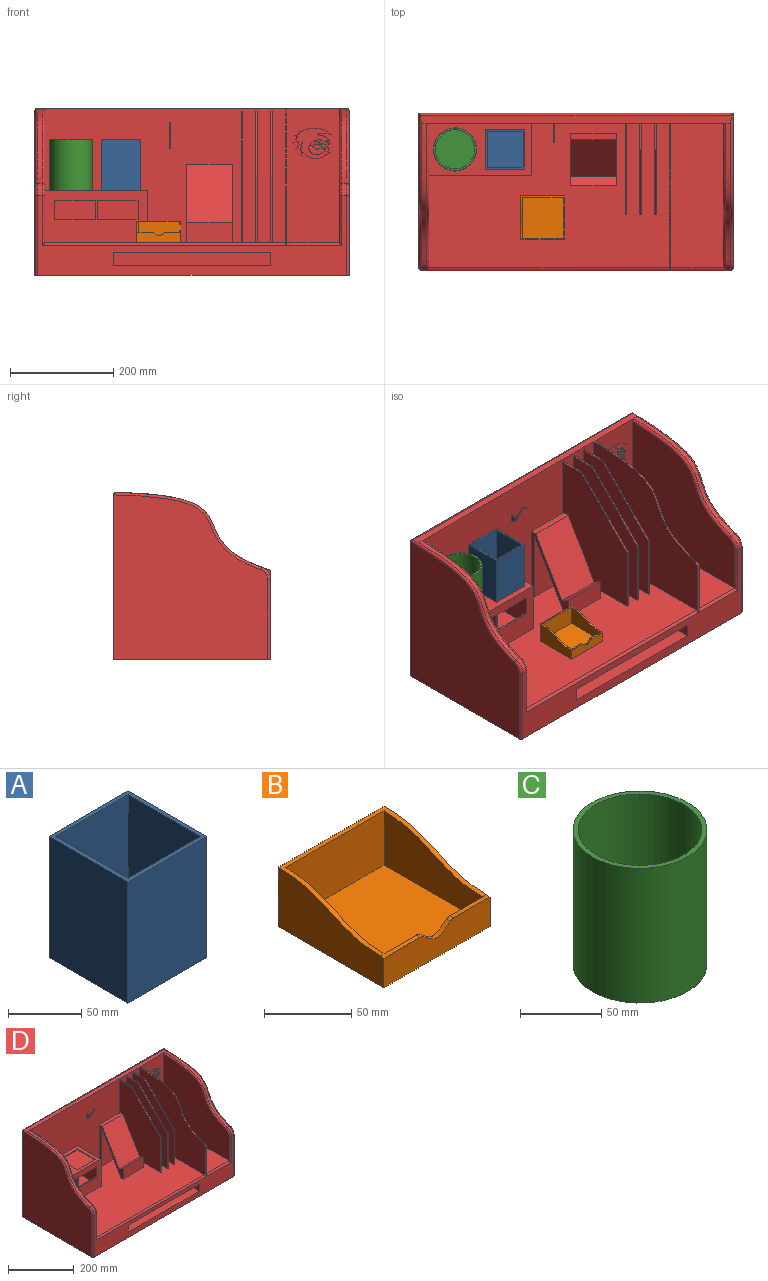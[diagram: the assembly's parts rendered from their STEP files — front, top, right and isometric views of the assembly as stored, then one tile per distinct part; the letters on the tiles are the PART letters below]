
ASSEMBLY  parts=4 mates=3
PART A: 11 faces, bbox 76.2x76.2x101.6 mm
  f0: plane 101.6x76.2mm, normal (-1,0,0), area 7741.9mm2, adj f1,f3,f4,f5
  f1: plane 101.6x76.2mm, normal (0,-1,0), area 7741.9mm2, adj f0,f2,f4,f5
  f2: plane 101.6x76.2mm, normal (1,0,0), area 7741.9mm2, adj f1,f3,f4,f5
  f3: plane 101.6x76.2mm, normal (0,1,0), area 7741.9mm2, adj f0,f2,f4,f5
  f4: plane 76.2x76.2mm, normal (0,0,1), area 927.4mm2, adj f0,f1,f2,f3,f6,f7,f8,f9
  f5: plane 76.2x76.2mm, normal (0,0,-1), area 5806.4mm2, adj f0,f1,f2,f3
  f6: plane 98.43x69.85mm, normal (1,0,0), area 6875mm2, adj f4,f7,f9,f10
  f7: plane 98.43x69.85mm, normal (0,1,0), area 6875mm2, adj f4,f6,f8,f10
  f8: plane 98.43x69.85mm, normal (-1,0,0), area 6875mm2, adj f4,f7,f9,f10
  f9: plane 98.43x69.85mm, normal (0,-1,0), area 6875mm2, adj f4,f6,f8,f10
  f10: plane 69.85x69.85mm, normal (0,0,1), area 4879mm2, adj f6,f7,f8,f9
PART B: 18 faces, bbox 85.7x85.7x41.3 mm
  f0: plane 79.38x17.46mm, normal (0,1,0), area 1283.4mm2, adj f7,f9,f10,f11,f13,f15,f16,f17
  f1: plane 85.73x41.28mm, normal (1,0,0), area 2661mm2, adj f2,f3,f5,f6,f14,f15
  f2: extruded ~85.73x82.55mm, area 797.9mm2, adj f1,f4,f5,f8,f9,f10,f12,f14
  f3: plane 85.73x20.64mm, normal (0,-1,0), area 1666.5mm2, adj f1,f4,f6,f11,f13,f15,f16,f17
  f4: plane 85.73x41.28mm, normal (-1,0,0), area 2661mm2, adj f2,f3,f5,f6,f12,f13
  f5: plane 85.73x41.28mm, normal (0,1,0), area 3538.3mm2, adj f1,f2,f4,f6
  f6: plane 85.73x85.73mm, normal (0,0,-1), area 7348.8mm2, adj f1,f3,f4,f5
  f7: plane 79.38x79.38mm, normal (0,0,1), area 6300.4mm2, adj f0,f8,f9,f10
  f8: plane 79.38x38.06mm, normal (0,-1,0), area 3021.2mm2, adj f2,f7,f9,f10
  f9: plane 85.73x38.1mm, normal (-1,0,0), area 2212.5mm2, adj f0,f2,f7,f8,f14
  f10: plane 85.73x38.1mm, normal (1,0,0), area 2212.5mm2, adj f0,f2,f7,f8,f12
  f11: extruded ~21.25x6.04mm, area 78.7mm2, adj f0,f3,f16,f17
  f12: plane 3.18x0.04mm, normal (0,-1,0), area 0.1mm2, adj f2,f4,f10,f13
  f13: plane 29.06x3.18mm, normal (0,0,1), area 92.3mm2, adj f0,f3,f4,f12,f16
  f14: plane 3.18x0.04mm, normal (0,-1,0), area 0.1mm2, adj f1,f2,f9,f15
  f15: plane 29.14x3.18mm, normal (0,0,1), area 92.5mm2, adj f0,f1,f3,f14,f17
  f16: cylinder r=5.08mm len=3.19mm, axis (0,-1,0), area 11mm2, adj f0,f3,f11,f13
  f17: cylinder r=5.08mm len=3.18mm, axis (0,-1,0), area 10.5mm2, adj f0,f3,f11,f15
PART C: 5 faces, bbox 82.6x82.6x101.6 mm
  f0: cylinder r=38.1mm len=98.43mm, axis (0,0,-1), area 23561.9mm2, adj f1,f4
  f1: plane 76.2x76.2mm, normal (0,0,1), area 4560.4mm2, adj f0
  f2: plane 82.55x82.55mm, normal (0,0,-1), area 5352.1mm2, adj f3
  f3: cylinder r=41.27mm len=101.6mm, axis (0,0,-1), area 26348.8mm2, adj f2,f4
  f4: plane 82.55x82.55mm, normal (0,0,1), area 791.7mm2, adj f0,f3
PART D: 129 faces, bbox 610.7x318.8x325.8 mm
  f0: plane 24.63x18.14mm, normal (-1,0,0), area 108.7mm2, adj f2,f127,f128
  f1: plane 24.63x18.14mm, normal (1,0,0), area 108.7mm2, adj f2,f125,f126
  f2: plane 472.26x260.81mm, normal (0,-1,0), area 98721.5mm2, adj f0,f1,f7,f8,f14,f15,f57,f59
  f3: plane 79.38x3.18mm, normal (0,0,1), area 252mm2, adj f79,f109,f110,f113
  f4: plane 79.38x3.18mm, normal (0,0,1), area 252mm2, adj f79,f103,f104,f107
  f5: plane 152.4x101.6mm, normal (-1,0,0), area 2847.1mm2, adj f7,f81,f82,f83,f84,f85,f86,f87
  f6: plane 152.4x101.6mm, normal (1,0,0), area 2847.1mm2, adj f7,f81,f82,f83,f84,f85,f86,f87
  f7: plane 466.73x280.67mm, normal (0,0,1), area 107438.7mm2, adj f2,f5,f6,f8,f15,f57,f58,f59
  f8: plane 280.69x255.29mm, normal (1,0,0), area 45920.9mm2, adj f2,f7,f79,f80,f88,f89,f91
  f9: plane 260.53x106.86mm, normal (0,-1,0), area 23716.6mm2, adj f13,f14,f16,f22,f33,f34,f35,f36
  f10: plane 319.37x299.72mm, normal (-1,0,0), area 80145.8mm2, adj f20,f21,f96,f97,f98,f99
  f11: plane 319.37x299.72mm, normal (1,0,0), area 80145.8mm2, adj f20,f21,f99,f100,f101,f102
  f12: plane 599.44x173.06mm, normal (0,-1,0), area 29355mm2, adj f15,f16,f17,f18,f21,f23,f24,f25
  f13: plane 280.69x255.29mm, normal (-1,0,0), area 56243.5mm2, adj f9,f22,f92,f93,f95
  f14: plane 604.6x15.06mm, normal (0,0,1), area 8412.6mm2, adj f2,f9,f25,f26,f27,f98,f99,f100
  f15: plane 285.75x265.43mm, normal (-1,0,0), area 58574mm2, adj f2,f7,f12,f25,f90
  f16: plane 285.75x265.43mm, normal (1,0,0), area 58574mm2, adj f9,f12,f22,f25,f94
  f17: plane 304.8x215.9mm, normal (0,0,1), area 65806.3mm2, adj f12,f19,f23,f24
  f18: plane 304.8x215.9mm, normal (0,0,-1), area 65806.3mm2, adj f12,f19,f23,f24
  f19: plane 304.8x25.4mm, normal (0,-1,0), area 7741.9mm2, adj f17,f18,f23,f24
  f20: plane 609.6x318.77mm, normal (0,1,0), area 194322.2mm2, adj f10,f11,f21,f99
  f21: plane 609.6x304.8mm, normal (0,0,-1), area 185795mm2, adj f10,f11,f12,f20,f96,f102
  f22: plane 280.67x101.6mm, normal (0,0,1), area 28516.1mm2, adj f9,f13,f16,f94
  f23: plane 215.9x25.4mm, normal (1,0,0), area 5483.9mm2, adj f12,f17,f18,f19
  f24: plane 215.9x25.4mm, normal (-1,0,0), area 5483.9mm2, adj f12,f17,f18,f19
  f25: extruded ~285.75x150.79mm, area 1094.7mm2, adj f12,f14,f15,f16
  f26: extruded ~268.97x145.16mm, area 2907.8mm2, adj f14,f29,f88,f98
  f27: extruded ~268.97x145.16mm, area 2907.8mm2, adj f14,f28,f92,f100
  f28: cylinder r=25.4mm len=23.89mm, axis (1,0,0), area 276.5mm2, adj f12,f27,f93,f101
  f29: cylinder r=25.4mm len=23.89mm, axis (1,0,0), area 276.5mm2, adj f12,f26,f89,f97
  f30: extruded ~3.81x2.23mm, area 13mm2, adj f52,f53,f56
  f31: extruded ~15.99x3.81mm, area 72.7mm2, adj f32,f49,f53,f55
  f32: extruded ~31.93x17.85mm, area 177.4mm2, adj f31,f49,f53,f55
  f33: extruded ~28.35x17.13mm, area 198.3mm2, adj f9,f34,f50,f53
  f34: extruded ~12.32x3.88mm, area 60.3mm2, adj f9,f33,f35,f53
  f35: extruded ~61.37x13.22mm, area 353.4mm2, adj f9,f34,f36,f53
  f36: extruded ~9.17x7.63mm, area 47.9mm2, adj f9,f35,f37,f53
  f37: extruded ~14.68x8.43mm, area 80mm2, adj f9,f36,f38,f53
  f38: extruded ~16.13x11.02mm, area 109.9mm2, adj f9,f37,f39,f53
  f39: extruded ~16.72x13.57mm, area 144.1mm2, adj f9,f38,f40,f53
  f40: extruded ~13.33x3.81mm, area 70.6mm2, adj f9,f39,f41,f53
  f41: extruded ~51.25x13.41mm, area 244mm2, adj f9,f40,f42,f53
  f42: extruded ~4.5x3.81mm, area 21.8mm2, adj f9,f41,f43,f53
  f43: extruded ~5.17x4mm, area 25.1mm2, adj f9,f42,f50,f53
  f44: extruded ~5.57x5.27mm, area 29.5mm2, adj f45,f51,f53,f54
  f45: extruded ~24.26x14.85mm, area 116.3mm2, adj f44,f46,f53,f54
  f46: extruded ~11.34x8.7mm, area 62.2mm2, adj f45,f47,f53,f54
  f47: extruded ~10.16x3.81mm, area 46.3mm2, adj f46,f48,f53,f54
  f48: extruded ~5.23x4.75mm, area 27mm2, adj f47,f51,f53,f54
  f49: extruded ~15.73x8.64mm, area 68.9mm2, adj f31,f32,f53,f55
  f50: extruded ~26.47x19.58mm, area 138mm2, adj f9,f33,f43,f53
  f51: extruded ~6x3.82mm, area 27.9mm2, adj f44,f48,f53,f54
  f52: extruded ~3.81x2.38mm, area 14.7mm2, adj f30,f53,f56
  f53: plane 74.8x59.57mm, normal (0,-1,0), area 2258.7mm2, adj f30,f31,f32,f33,f34,f35,f36,f37
  f54: plane 29.84x14.86mm, normal (0,-1,0), area 151.1mm2, adj f44,f45,f46,f47,f48,f51
  f55: plane 31.99x17.9mm, normal (0,-1,0), area 322.3mm2, adj f31,f32,f49
  f56: plane 2.94x2.91mm, normal (0,-1,0), area 3.4mm2, adj f30,f52
  f57: plane 254x177.8mm, normal (-1,0,0), area 37095.6mm2, adj f2,f7,f58,f60,f71,f72,f73
  f58: plane 124.9x3.18mm, normal (0,-1,0), area 396.5mm2, adj f7,f57,f59,f73
  f59: plane 254x177.8mm, normal (1,0,0), area 37095.6mm2, adj f2,f7,f58,f60,f71,f72,f73
  f60: plane 48.7x3.18mm, normal (0,0,1), area 154.6mm2, adj f2,f57,f59,f72
  f61: plane 254x177.8mm, normal (-1,0,0), area 37095.6mm2, adj f2,f7,f62,f64,f70,f74,f75
  f62: plane 124.9x3.18mm, normal (0,-1,0), area 396.5mm2, adj f7,f61,f63,f75
  f63: plane 254x177.8mm, normal (1,0,0), area 37095.6mm2, adj f2,f7,f62,f64,f70,f74,f75
  f64: plane 48.7x3.18mm, normal (0,0,1), area 154.6mm2, adj f2,f61,f63,f74
  f65: plane 254x177.8mm, normal (-1,0,0), area 37095.6mm2, adj f2,f7,f66,f68,f69,f76,f77
  f66: plane 124.9x3.18mm, normal (0,-1,0), area 396.5mm2, adj f7,f65,f67,f77
  f67: plane 254x177.8mm, normal (1,0,0), area 37095.6mm2, adj f2,f7,f66,f68,f69,f76,f77
  f68: plane 48.7x3.18mm, normal (0,0,1), area 154.6mm2, adj f2,f65,f67,f76
  f69: plane 124.02x124.02mm, normal (0,-0.71,0.71), area 556.9mm2, adj f65,f67,f76,f77
  f70: plane 124.02x124.02mm, normal (0,-0.71,0.71), area 556.9mm2, adj f61,f63,f74,f75
  f71: plane 124.02x124.02mm, normal (0,-0.71,0.71), area 556.9mm2, adj f57,f59,f72,f73
  f72: cylinder r=5.08mm len=3.59mm, axis (-1,0,0), area 12.7mm2, adj f57,f59,f60,f71
  f73: cylinder r=5.08mm len=3.59mm, axis (1,0,0), area 12.7mm2, adj f57,f58,f59,f71
  f74: cylinder r=5.08mm len=3.59mm, axis (-1,0,0), area 12.7mm2, adj f61,f63,f64,f70
  f75: cylinder r=5.08mm len=3.59mm, axis (1,0,0), area 12.7mm2, adj f61,f62,f63,f70
  f76: cylinder r=5.08mm len=3.59mm, axis (-1,0,0), area 12.7mm2, adj f65,f67,f68,f69
  f77: cylinder r=5.08mm len=3.59mm, axis (1,0,0), area 12.7mm2, adj f65,f66,f67,f69
  f78: plane 101.6x101.6mm, normal (1,0,0), area 10322.6mm2, adj f2,f7,f79,f80
  f79: plane 200.03x101.6mm, normal (0,-1,0), area 14274.2mm2, adj f3,f4,f7,f8,f78,f80,f103,f104
  f80: plane 200.03x101.6mm, normal (0,0,1), area 8802.9mm2, adj f2,f8,f78,f79,f115,f117,f118,f119
  f81: plane 88.9x39.06mm, normal (0,-1,0), area 3472.1mm2, adj f5,f6,f7,f85
  f82: plane 152.4x88.9mm, normal (0,1,0), area 13548.4mm2, adj f5,f6,f7,f83
  f83: plane 88.9x12.7mm, normal (0,0,1), area 1128.8mm2, adj f5,f6,f82,f84
  f84: plane 123.5x88.9mm, normal (0,-0.87,0.5), area 12678.1mm2, adj f5,f6,f83,f85
  f85: plane 88.9x17.6mm, normal (0,0.5,0.87), area 1806.4mm2, adj f5,f6,f81,f84
  f86: plane 145.95x88.9mm, normal (0,0.87,-0.5), area 14982.6mm2, adj f5,f6,f7,f87
  f87: plane 145.95x88.9mm, normal (0,-1,0), area 12975.3mm2, adj f5,f6,f7,f86
  f88: bspline ~284.98x153.73mm, area 2604.7mm2, adj f2,f8,f26,f89
  f89: torus R=20.32mm, axis (-1,0,0), area 230.2mm2, adj f8,f29,f88,f91
  f90: cylinder r=5.08mm len=471.81mm, axis (-1,0,0), area 3744.6mm2, adj f7,f12,f15,f91
  f91: cylinder r=5.08mm len=96.38mm, axis (0,0,-1), area 748.8mm2, adj f8,f12,f89,f90
  f92: bspline ~284.98x153.73mm, area 2604.7mm2, adj f9,f13,f27,f93
  f93: torus R=20.32mm, axis (-1,0,0), area 230.2mm2, adj f13,f28,f92,f95
  f94: cylinder r=5.08mm len=106.68mm, axis (-1,0,0), area 831mm2, adj f12,f16,f22,f95
  f95: cylinder r=5.08mm len=96.38mm, axis (0,0,1), area 748.8mm2, adj f12,f13,f93,f94
  f96: cylinder r=5.08mm len=154.8mm, axis (0,0,-1), area 1235.3mm2, adj f10,f12,f21,f97
  f97: torus R=20.32mm, axis (1,0,0), area 230.2mm2, adj f10,f29,f96,f98
  f98: bspline ~309.15x154.47mm, area 2716.6mm2, adj f10,f14,f26,f97,f99
  f99: cylinder r=5.08mm len=609.6mm, axis (1,0,0), area 4844.6mm2, adj f10,f11,f14,f20,f98,f100
  f100: bspline ~309.15x154.47mm, area 2716.6mm2, adj f11,f14,f27,f99,f101
  f101: torus R=20.32mm, axis (1,0,0), area 230.2mm2, adj f11,f28,f100,f102
  f102: cylinder r=5.08mm len=154.8mm, axis (0,0,1), area 1235.3mm2, adj f11,f12,f21,f101
  f103: plane 79.38x63.5mm, normal (1,0,0), area 4959.7mm2, adj f4,f79,f105,f106,f107,f108
  f104: plane 79.38x63.5mm, normal (-1,0,0), area 4959.7mm2, adj f4,f79,f105,f106,f107,f108
  f105: plane 79.38x79.38mm, normal (0,0,-1), area 6300.4mm2, adj f79,f103,f104,f106
  f106: plane 79.38x63.5mm, normal (0,-1,0), area 5040.3mm2, adj f103,f104,f105,f108
  f107: plane 79.38x25.4mm, normal (0,1,0), area 2016.1mm2, adj f4,f103,f104,f108
  f108: plane 79.38x76.2mm, normal (0,0,1), area 6048.4mm2, adj f103,f104,f106,f107
  f109: plane 79.38x63.5mm, normal (1,0,0), area 4959.7mm2, adj f3,f79,f111,f112,f113,f114
  f110: plane 79.38x63.5mm, normal (-1,0,0), area 4959.7mm2, adj f3,f79,f111,f112,f113,f114
  f111: plane 79.38x79.38mm, normal (0,0,-1), area 6300.4mm2, adj f79,f109,f110,f112
  f112: plane 79.38x63.5mm, normal (0,-1,0), area 5040.3mm2, adj f109,f110,f111,f114
  f113: plane 79.38x25.4mm, normal (0,1,0), area 2016.1mm2, adj f3,f109,f110,f114
  f114: plane 79.38x76.2mm, normal (0,0,1), area 6048.4mm2, adj f109,f110,f112,f113
  f115: cylinder r=41.91mm len=83.82mm, axis (0,0,1), area 836.1mm2, adj f80,f116
  f116: plane 83.82x83.82mm, normal (0,0,1), area 5518mm2, adj f115
  f117: plane 77.47x3.18mm, normal (1,0,0), area 246mm2, adj f80,f118,f120,f121
  f118: plane 77.47x3.18mm, normal (0,1,0), area 246mm2, adj f80,f117,f119,f121
  f119: plane 77.47x3.18mm, normal (-1,0,0), area 246mm2, adj f80,f118,f120,f121
  f120: plane 77.47x3.18mm, normal (0,-1,0), area 246mm2, adj f80,f117,f119,f121
  f121: plane 77.47x77.47mm, normal (0,0,1), area 6001.6mm2, adj f117,f118,f119,f120
  f122: plane 2.65x2.44mm, normal (0,0,1), area 3.7mm2, adj f123,f124,f125,f126,f127,f128
  f123: extruded ~37.09x35.81mm, area 36.1mm2, adj f2,f122,f125,f127
  f124: extruded ~50.8x38.1mm, area 41.9mm2, adj f2,f122,f126,f128
  f125: bspline ~39.16x38.66mm, area 95.5mm2, adj f1,f2,f122,f123,f126
  f126: bspline ~52.19x39mm, area 110.6mm2, adj f1,f2,f122,f124,f125
  f127: bspline ~39.16x38.66mm, area 95.5mm2, adj f0,f2,f122,f123,f128
  f128: bspline ~52.13x38.74mm, area 110.6mm2, adj f0,f2,f122,f124,f127
PLACE A t=(-139.75,81.26,81.78)mm
PLACE B t=(-66.31,-50.17,-13.47)mm
PLACE C t=(-236.52,82.99,81.78)mm
PLACE D t=(7.91,4.06,-80.15)mm fixed
MATE planar B.f6 <-> D.f7  axis (0,0,-1) through (-65.99,-49.58,-16.65)mm
MATE fastened A.f5 <-> D.f121  axis (0,0,-1) through (-139.36,82.99,81.78)mm
MATE fastened C.f0 <-> D.f115  axis (0,0,-1) through (-236.52,82.99,81.78)mm
